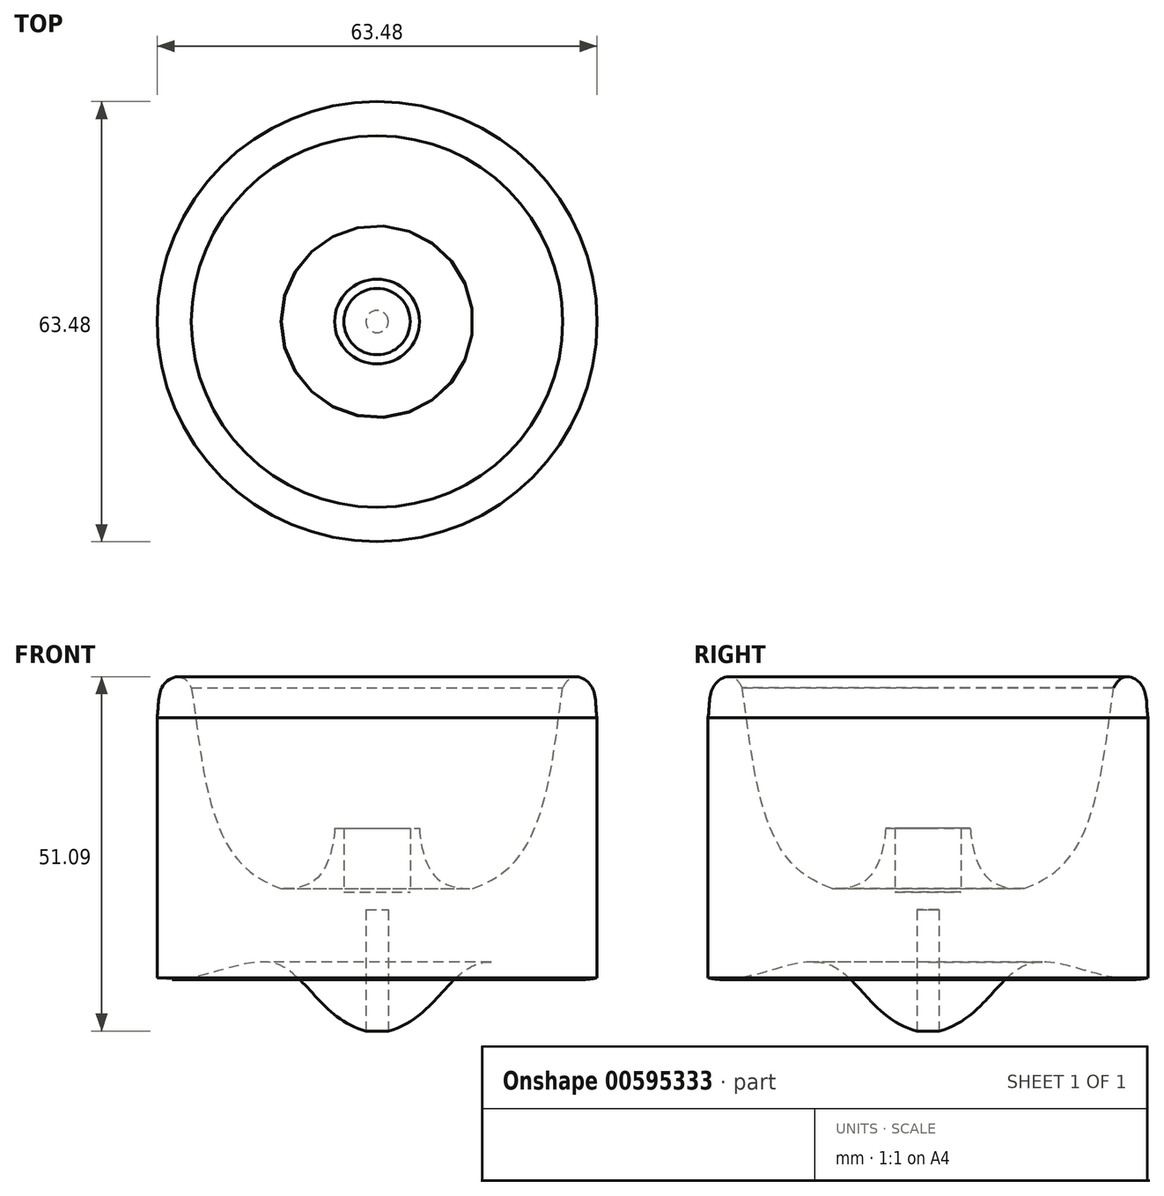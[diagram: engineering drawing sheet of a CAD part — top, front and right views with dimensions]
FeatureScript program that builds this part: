
annotation { "Feature Type Name" : "Feature", "Feature Type Description" : "" }
export const myFeature = defineFeature(function(context is Context, id is Id, definition is map)
    precondition{}
    {
        {
            var Q0;
            Q0=qCreatedBy(makeId("Front.planeOp"),FACE);
            var sketch = newSketch(context, id + "F0", { "sketchPlane" : qUnion([Q0])});
            skLineSegment(sketch, "E0", {"start": v(1.6, 0) * mm, "end": v(1.6, 17.48) * mm});
            skLineSegment(sketch, "E1", {"start": v(1.6, 17.48) * mm, "end": v(0, 17.48) * mm});
            skPoint(sketch, "E2.endSnap0", {"position": v(25.4, 40.03) * mm});
            skPoint(sketch, "E3.endSnap0", {"position": v(25.4, 17.84) * mm});
            skFitSpline(sketch, "E4", {"points": [v(26.8, 49.49) * mm, v(20.27, 24.9) * mm, v(4.78, 19.2) * mm], "startDerivative": vector(-6.23, -37.78) * mm, "endDerivative": vector(-34.4, 0) * mm});
            skLineSegment(sketch, "E5", {"start": v(0, 17.48) * mm, "end": v(0, 20.03) * mm});
            skLineSegment(sketch, "E6", {"start": v(0, 20.03) * mm, "end": v(4.78, 20.03) * mm});
            skLineSegment(sketch, "E7", {"start": v(4.78, 29.23) * mm, "end": v(4.78, 20.03) * mm});
            skFitSpline(sketch, "E8", {"points": [v(31.74, 45.2) * mm, v(30.78, 49.95) * mm, v(26.8, 49.49) * mm], "startDerivative": vector(-1.75, 9.24) * mm, "endDerivative": vector(-6.76, -15.45) * mm});
            skLineSegment(sketch, "E9", {"start": v(31.74, 45.2) * mm, "end": v(31.74, 7.68) * mm});
            skLineSegment(sketch, "E10", {"start": v(4.78, 29.23) * mm, "end": v(6.11, 29.23) * mm});
            skFitSpline(sketch, "E11", {"points": [v(6.11, 29.23) * mm, v(9.11, 21.66) * mm, v(13.8, 20.54) * mm, v(13.85, 20.55) * mm], "startDerivative": vector(0.54, -11.8) * mm, "endDerivative": vector(0.5, 0.58) * mm});
            skLineSegment(sketch, "E12", {"start": v(1.6, 0) * mm, "end": v(0, 0) * mm});
            skFitSpline(sketch, "E13", {"points": [v(1.6, 0) * mm, v(14.77, 9.76) * mm, v(31.74, 7.68) * mm], "startDerivative": vector(39.06, 9.96) * mm, "endDerivative": vector(32.34, 8.25) * mm});
            skSolve(sketch);
        }
        {
            var Q0;
            Q0=makeQuery(id+"F0.imprint","IMPRINT",FACE,{"disambiguationData":[TD([[makeQuery(id+"F0.imprint","IMPRINT",EDGE,{"derivedFrom":sQuery(id+"F0.wireOp",EDGE,"E7")}),1.0]])]});
            var Q1;
            Q1=makeQuery(id+"F0.imprint","IMPRINT",FACE,{"disambiguationData":[TD([[makeQuery(id+"F0.imprint","IMPRINT",EDGE,{"derivedFrom":sQuery(id+"F0.wireOp",EDGE,"E0")}),-1.0]])]});
            var Q2;
            Q2=sQuery(id+"F0.wireOp",EDGE,"E5");
            revolve(context, id + "F1", {"entities" : qUnion([Q0, Q1]), "axis" : qUnion([Q2]), "revolveType" : RevolveType.FULL});
        }
    });
